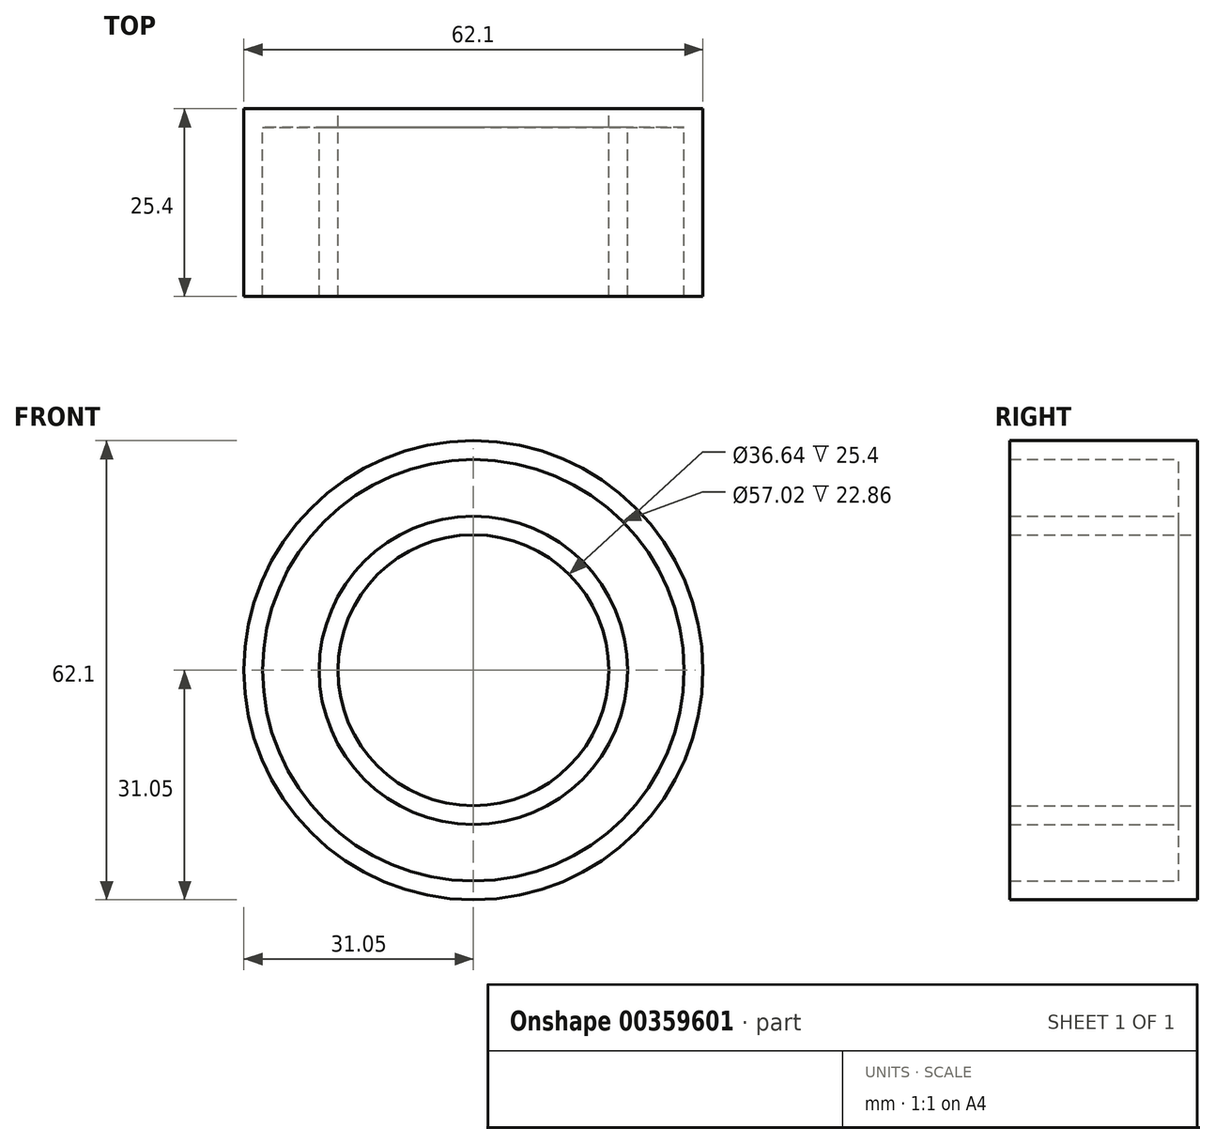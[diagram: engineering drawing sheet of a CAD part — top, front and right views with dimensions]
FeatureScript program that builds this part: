
annotation { "Feature Type Name" : "Feature", "Feature Type Description" : "" }
export const myFeature = defineFeature(function(context is Context, id is Id, definition is map)
    precondition{}
    {
        {
            var Q0;
            Q0=qCreatedBy(makeId("Front.planeOp"),FACE);
            var sketch = newSketch(context, id + "F0", { "sketchPlane" : qUnion([Q0])});
            skCircle(sketch, "E0", {"center": v(0, 0) * mm, "radius": 31.05 * mm});
            skCircle(sketch, "E1", {"center": v(0, 0) * mm, "radius": 18.32 * mm});
            skSolve(sketch);
        }
        {
            var Q0;
            Q0 = qSketchRegion(id + "F0", true);
            extrude(context, id + "F1", {"entities" : qUnion([Q0]), "depth" : 25.4 * mm});
        }
        {
            var Q0;
            Q0=makeQuery(id+"F1.opExtrude","CAP_FACE",FACE,{"disambiguationData":[OSD([sQuery(id+"F0.wireOp",EDGE,"E0"),sQuery(id+"F0.wireOp",EDGE,"E1")])],"isStart":false});
            shell(context, id + "F2", {"entities" : qUnion([Q0]), "thickness" : 2.54 * mm});
        }
    });
